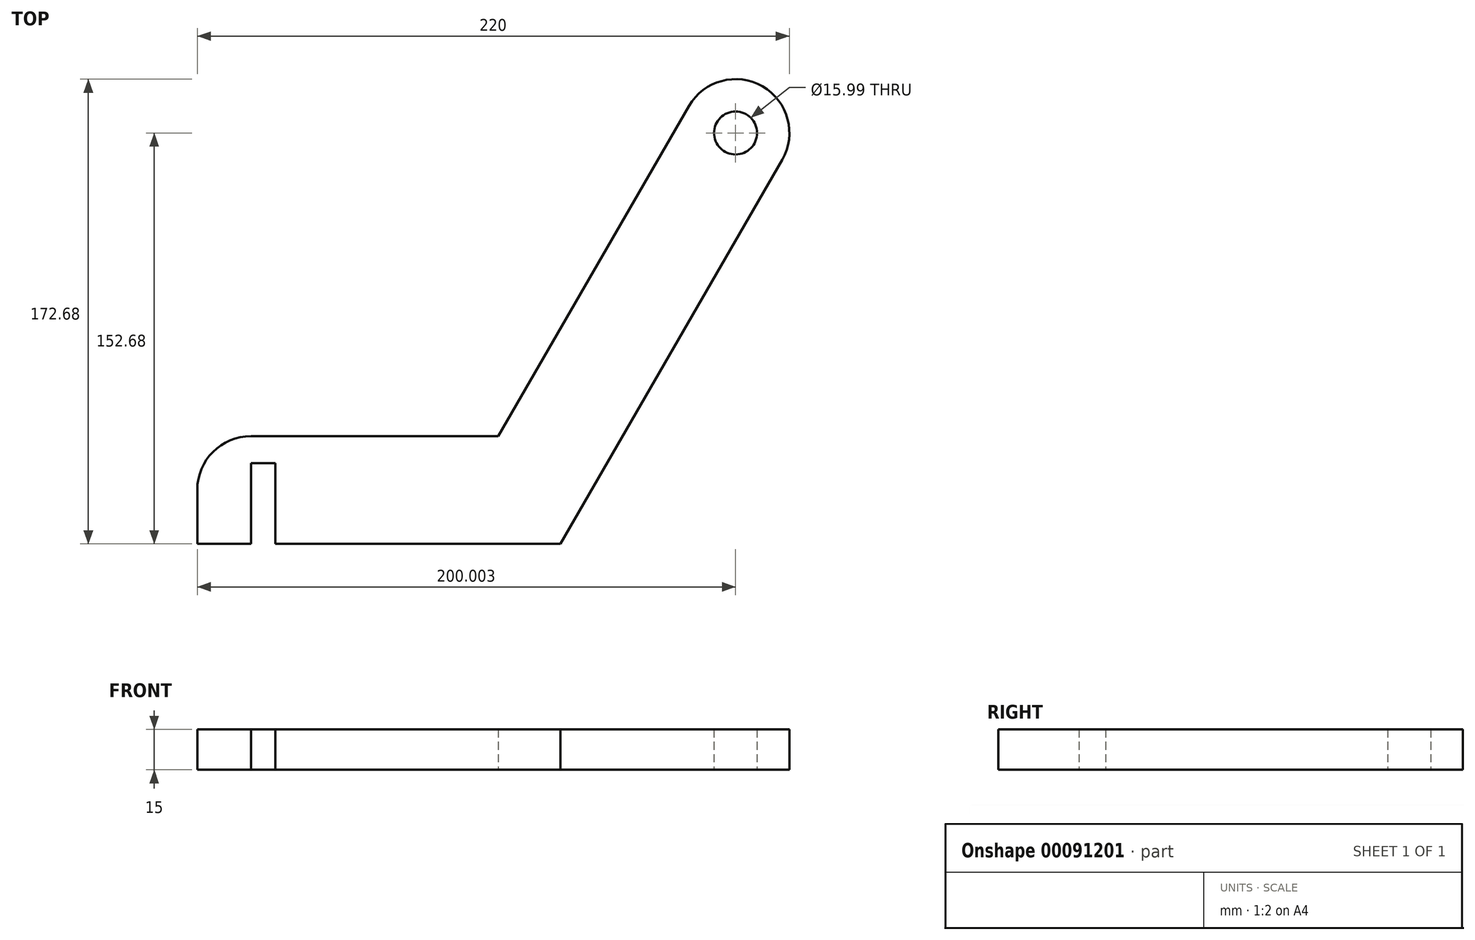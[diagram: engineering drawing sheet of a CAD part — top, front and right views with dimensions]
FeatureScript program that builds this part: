
annotation { "Feature Type Name" : "Feature", "Feature Type Description" : "" }
export const myFeature = defineFeature(function(context is Context, id is Id, definition is map)
    precondition{}
    {
        {
            var Q0;
            Q0=qCreatedBy(makeId("Top.planeOp"),FACE);
            var sketch = newSketch(context, id + "F0", { "sketchPlane" : qUnion([Q0])});
            skLineSegment(sketch, "E0.bottom", {"start": v(-31.58, 0) * mm, "end": v(83.37, 0) * mm});
            skLineSegment(sketch, "E0.top", {"start": v(-51.58, -40) * mm, "end": v(83.37, -40) * mm});
            skLineSegment(sketch, "E0.left", {"start": v(-51.58, -20) * mm, "end": v(-51.58, -40) * mm});
            skLineSegment(sketch, "E0.right", {"start": v(83.37, 0) * mm, "end": v(83.37, -40) * mm});
            skLineSegment(sketch, "E1.bottom", {"start": v(-31.58, -40) * mm, "end": v(-22.58, -40) * mm});
            skLineSegment(sketch, "E1.top", {"start": v(-31.58, -10) * mm, "end": v(-22.58, -10) * mm});
            skLineSegment(sketch, "E1.left", {"start": v(-31.58, -40) * mm, "end": v(-31.58, -10) * mm});
            skLineSegment(sketch, "E1.right", {"start": v(-22.58, -40) * mm, "end": v(-22.58, -10) * mm});
            skPoint(sketch, "E2.visualSharp", {"position": v(-51.58, 0) * mm});
            skArc(sketch, "E2.filletArc", {"start": v(-31.58, 0) * mm, "mid": v(-45.72, -5.86) * mm, "end": v(-51.58, -20) * mm});
            skLineSegment(sketch, "E3", {"start": v(60.27, 0) * mm, "end": v(131.1, 122.68) * mm});
            skLineSegment(sketch, "E4", {"start": v(83.37, -40) * mm, "end": v(165.74, 102.68) * mm});
            skLineSegment(sketch, "E5", {"start": v(158.42, 130) * mm, "end": v(158.42, 130) * mm});
            skPoint(sketch, "E6.visualSharp", {"position": v(141.1, 140) * mm});
            skArc(sketch, "E6.filletArc", {"start": v(158.42, 130) * mm, "mid": v(143.25, 132) * mm, "end": v(131.1, 122.68) * mm});
            skPoint(sketch, "E7.visualSharp", {"position": v(175.74, 120) * mm});
            skArc(sketch, "E7.filletArc", {"start": v(165.74, 102.68) * mm, "mid": v(167.74, 117.86) * mm, "end": v(158.42, 130) * mm});
            skCircle(sketch, "E8", {"center": v(148.42, 112.68) * mm, "radius": 8 * mm});
            skLineSegment(sketch, "E9", {"start": v(83.37, -20) * mm, "end": v(83.37, 0) * mm});
            skLineSegment(sketch, "E10", {"start": v(83.37, 0) * mm, "end": v(83.37, 0) * mm});
            skSolve(sketch);
        }
        {
            var Q0;
            {var subQ8=sQuery(id+"F0.wireOp",EDGE,"E0.left");Q0=makeQuery(id+"F0.imprint","IMPRINT",FACE,{"disambiguationData":[TD([[makeQuery(id+"F0.imprint","IMPRINT",EDGE,{"derivedFrom":subQ8}),1.0]])]});}
            var Q1;
            {var subQ0=sQuery(id+"F0.wireOp",EDGE,"E9");Q1=makeQuery(id+"F0.imprint","IMPRINT",FACE,{"disambiguationData":[TD([[makeQuery(id+"F0.imprint","IMPRINT",EDGE,{"derivedFrom":subQ0}),1.0]])]});}
            var Q2;
            {var subQ4=sQuery(id+"F0.wireOp",EDGE,"E6.filletArc");Q2=makeQuery(id+"F0.imprint","IMPRINT",FACE,{"disambiguationData":[TD([[makeQuery(id+"F0.imprint","IMPRINT",EDGE,{"derivedFrom":subQ4}),1.0]])]});}
            var Q3;
            {var subQ0=sQuery(id+"F0.wireOp",EDGE,"KlgkAUIO-qzU3-4CDe-aNye-TUUGqOHMVw3l");Q3=makeQuery(id+"F0.imprint","IMPRINT",FACE,{"disambiguationData":[TD([[makeQuery(id+"F0.imprint","IMPRINT",EDGE,{"derivedFrom":subQ0}),1.0]])]});}
            var Q4;
            {var subQ0=sQuery(id+"F0.wireOp",EDGE,"tsqzxqXg-OxR9-taaD-UKGH-81XYNMQX3zTJ");Q4=makeQuery(id+"F0.imprint","IMPRINT",FACE,{"disambiguationData":[TD([[makeQuery(id+"F0.imprint","IMPRINT",EDGE,{"derivedFrom":subQ0}),1.0]])]});}
            var Q5;
            {var subQ1=sQuery(id+"F0.wireOp",EDGE,"E5");Q5=makeQuery(id+"F0.imprint","IMPRINT",FACE,{"disambiguationData":[TD([[makeQuery(id+"F0.imprint","IMPRINT",EDGE,{"derivedFrom":subQ1}),-1.0]])]});}
            var Q6;
            {var subQ6=sQuery(id+"F0.wireOp",EDGE,"E4");Q6=makeQuery(id+"F0.imprint","IMPRINT",FACE,{"disambiguationData":[TD([[makeQuery(id+"F0.imprint","IMPRINT",EDGE,{"derivedFrom":subQ6}),1.0]])]});}
            extrude(context, id + "F1", {"entities" : qUnion([Q0, Q1, Q2, Q3, Q4, Q5, Q6]), "depth" : 15 * mm});
        }
    });
